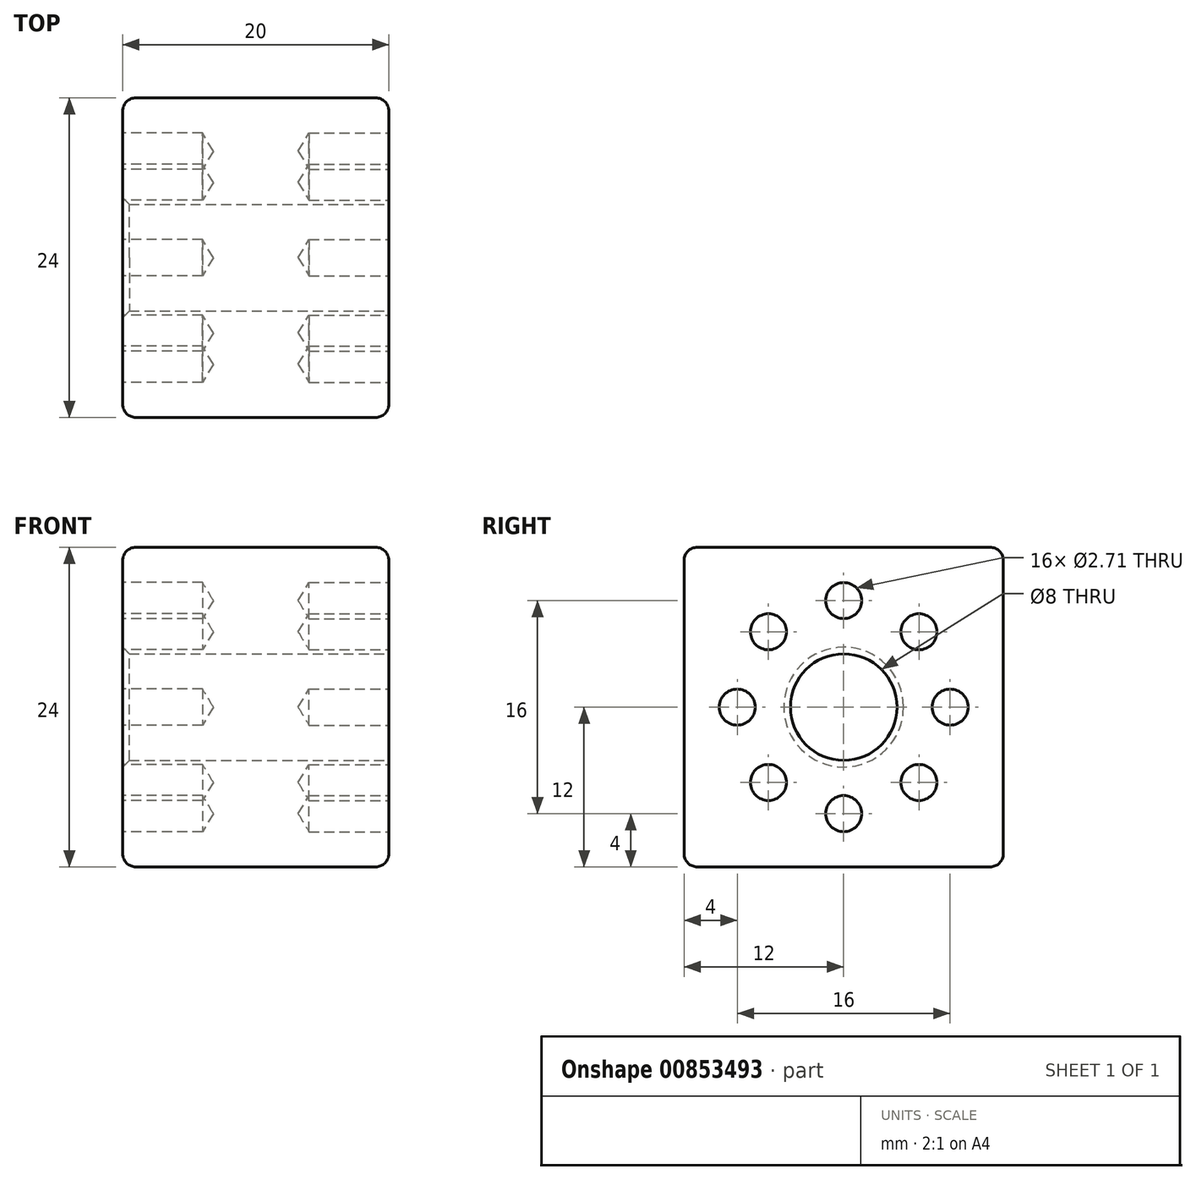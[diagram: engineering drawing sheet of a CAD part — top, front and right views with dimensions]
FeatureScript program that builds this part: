
annotation { "Feature Type Name" : "Feature", "Feature Type Description" : "" }
export const myFeature = defineFeature(function(context is Context, id is Id, definition is map)
    precondition{}
    {
        {
            var Q0;
            Q0=qCreatedBy(makeId("Top.planeOp"),FACE);
            var sketch = newSketch(context, id + "F0", { "sketchPlane" : qUnion([Q0])});
            skLineSegment(sketch, "E0.bottom", {"start": v(10, -12) * mm, "end": v(-10, -12) * mm});
            skLineSegment(sketch, "E0.top", {"start": v(10, 12) * mm, "end": v(-10, 12) * mm});
            skLineSegment(sketch, "E0.left", {"start": v(10, -12) * mm, "end": v(10, 12) * mm});
            skLineSegment(sketch, "E0.right", {"start": v(-10, -12) * mm, "end": v(-10, 12) * mm});
            skPoint(sketch, "E0.middle", {"position": v(0, 0) * mm});
            skSolve(sketch);
        }
        {
            var Q0;
            Q0 = qSketchRegion(id + "F0", true);
            extrude(context, id + "F1", {"entities" : qUnion([Q0]), "depth" : 24 * mm, "offsetDistance" : 25.4 * mm});
        }
        {
            var Q0;
            Q0=makeQuery(id+"F1.opExtrude","SWEPT_FACE",FACE,{"disambiguationData":[OSD([sQuery(id+"F0.wireOp",EDGE,"E0.left")])]});
            var sketch = newSketch(context, id + "F2", { "sketchPlane" : qUnion([Q0])});
            skCircle(sketch, "E1", {"center": v(0, 12) * mm, "radius": 4 * mm});
            skSolve(sketch);
        }
        {
            var Q0;
            Q0 = qSketchRegion(id + "F2", true);
            extrude(context, id + "F3", {"entities" : qUnion([Q0]), "operationType" : NewBodyOperationType.REMOVE, "endBound" : BoundingType.THROUGH_ALL, "oppositeDirection" : true, "depth" : 20 * mm, "offsetDistance" : 25.4 * mm});
        }
        {
            var Q0;
            Q0=makeQuery(id+"F1.opExtrude","SWEPT_FACE",FACE,{"disambiguationData":[OSD([sQuery(id+"F0.wireOp",EDGE,"E0.left")])]});
            var sketch = newSketch(context, id + "F4", { "sketchPlane" : qUnion([Q0])});
            skCircle(sketch, "E2.cCircle", {"center": v(0, 12) * mm, "radius": 8 * mm, "construction": true});
            skLineSegment(sketch, "E2.0", {"start": v(0, 4) * mm, "end": v(-5.66, 6.34) * mm, "construction": true});
            skLineSegment(sketch, "E2.1", {"start": v(-5.66, 6.34) * mm, "end": v(-8, 12) * mm, "construction": true});
            skLineSegment(sketch, "E2.2", {"start": v(-8, 12) * mm, "end": v(-5.66, 17.66) * mm, "construction": true});
            skLineSegment(sketch, "E2.3", {"start": v(-5.66, 17.66) * mm, "end": v(0, 20) * mm, "construction": true});
            skLineSegment(sketch, "E2.4", {"start": v(0, 20) * mm, "end": v(5.66, 17.66) * mm, "construction": true});
            skLineSegment(sketch, "E2.5", {"start": v(5.66, 17.66) * mm, "end": v(8, 12) * mm, "construction": true});
            skLineSegment(sketch, "E2.6", {"start": v(8, 12) * mm, "end": v(5.66, 6.34) * mm, "construction": true});
            skLineSegment(sketch, "E2.7", {"start": v(5.66, 6.34) * mm, "end": v(0, 4) * mm, "construction": true});
            skPoint(sketch, "E3", {"position": v(0, 20) * mm});
            skPoint(sketch, "E4", {"position": v(5.66, 17.66) * mm});
            skPoint(sketch, "E5", {"position": v(8, 12) * mm});
            skPoint(sketch, "E6", {"position": v(5.66, 6.34) * mm});
            skPoint(sketch, "E7", {"position": v(0, 4) * mm});
            skPoint(sketch, "E8", {"position": v(-5.66, 6.34) * mm});
            skPoint(sketch, "E9", {"position": v(-8, 12) * mm});
            skPoint(sketch, "E10", {"position": v(-5.66, 17.66) * mm});
            skSolve(sketch);
        }
        {
            var Q0;
            Q0=sQuery(id+"F4.wireOp",VERTEX,"E3");
            var Q1;
            Q1=sQuery(id+"F4.wireOp",VERTEX,"E4");
            var Q2;
            Q2=sQuery(id+"F4.wireOp",VERTEX,"E5");
            var Q3;
            Q3=sQuery(id+"F4.wireOp",VERTEX,"E6");
            var Q4;
            Q4=sQuery(id+"F4.wireOp",VERTEX,"E7");
            var Q5;
            Q5=sQuery(id+"F4.wireOp",VERTEX,"E8");
            var Q6;
            Q6=sQuery(id+"F4.wireOp",VERTEX,"E9");
            var Q7;
            Q7=sQuery(id+"F4.wireOp",VERTEX,"E10");
            var Q8;
            Q8=makeQuery(id+"F1.opExtrude","SWEPT_BODY",BODY,{"disambiguationData":[OSD([sQuery(id+"F0.wireOp",EDGE,"E0.bottom"),sQuery(id+"F0.wireOp",EDGE,"E0.top"),sQuery(id+"F0.wireOp",EDGE,"E0.left"),sQuery(id+"F0.wireOp",EDGE,"E0.right")])]});
            hole(context, id + "F5", {"style" : HoleStyle.SIMPLE, "endStyle" : HoleEndStyle.BLIND, "standardTappedOrClearance" : lookupTablePath({ "standard" : "ANSI", "engagement" : "75%", "pitch" : "32 tpi", "size" : "#6", "type" : "Tapped" }), "standardBlindInLast" : lookupTablePath({ "standard" : "ANSI", "engagement" : "75%", "pitch" : "32 tpi", "size" : "#6", "type" : "Tapped" }), "holeDiameter" : 2.7 * mm, "majorDiameter" : 3.5 * mm, "showTappedDepth" : true, "holeDepth" : 6 * mm, "isTappedThrough" : true, "tappedDepth" : 3.62 * mm, "tapClearance" : 3, "locations" : qUnion([Q0, Q1, Q2, Q3, Q4, Q5, Q6, Q7]), "scope" : qUnion([Q8])});
        }
        {
            var Q0;
            Q0=makeQuery(id+"F1.opExtrude","SWEPT_FACE",FACE,{"disambiguationData":[OSD([sQuery(id+"F0.wireOp",EDGE,"E0.right")])]});
            var sketch = newSketch(context, id + "F6", { "sketchPlane" : qUnion([Q0])});
            skCircle(sketch, "E11.cCircle", {"center": v(0, 12) * mm, "radius": 8 * mm, "construction": true});
            skLineSegment(sketch, "E11.0", {"start": v(0, 4) * mm, "end": v(-5.66, 6.34) * mm, "construction": true});
            skLineSegment(sketch, "E11.1", {"start": v(-5.66, 6.34) * mm, "end": v(-8, 12) * mm, "construction": true});
            skLineSegment(sketch, "E11.2", {"start": v(-8, 12) * mm, "end": v(-5.66, 17.66) * mm, "construction": true});
            skLineSegment(sketch, "E11.3", {"start": v(-5.66, 17.66) * mm, "end": v(0, 20) * mm, "construction": true});
            skLineSegment(sketch, "E11.4", {"start": v(0, 20) * mm, "end": v(5.66, 17.66) * mm, "construction": true});
            skLineSegment(sketch, "E11.5", {"start": v(5.66, 17.66) * mm, "end": v(8, 12) * mm, "construction": true});
            skLineSegment(sketch, "E11.6", {"start": v(8, 12) * mm, "end": v(5.66, 6.34) * mm, "construction": true});
            skLineSegment(sketch, "E11.7", {"start": v(5.66, 6.34) * mm, "end": v(0, 4) * mm, "construction": true});
            skPoint(sketch, "E12", {"position": v(0, 20) * mm});
            skPoint(sketch, "E13", {"position": v(5.66, 17.66) * mm});
            skPoint(sketch, "E14", {"position": v(8, 12) * mm});
            skPoint(sketch, "E15", {"position": v(5.66, 6.34) * mm});
            skPoint(sketch, "E16", {"position": v(0, 4) * mm});
            skPoint(sketch, "E17", {"position": v(-5.66, 6.34) * mm});
            skPoint(sketch, "E18", {"position": v(-8, 12) * mm});
            skPoint(sketch, "E19", {"position": v(-5.66, 17.66) * mm});
            skSolve(sketch);
        }
        {
            var Q0;
            Q0=sQuery(id+"F6.wireOp",VERTEX,"E12");
            var Q1;
            Q1=sQuery(id+"F6.wireOp",VERTEX,"E13");
            var Q2;
            Q2=sQuery(id+"F6.wireOp",VERTEX,"E14");
            var Q3;
            Q3=sQuery(id+"F6.wireOp",VERTEX,"E15");
            var Q4;
            Q4=sQuery(id+"F6.wireOp",VERTEX,"E16");
            var Q5;
            Q5=sQuery(id+"F6.wireOp",VERTEX,"E17");
            var Q6;
            Q6=sQuery(id+"F6.wireOp",VERTEX,"E18");
            var Q7;
            Q7=sQuery(id+"F6.wireOp",VERTEX,"E19");
            var Q8;
            Q8=makeQuery(id+"F1.opExtrude","SWEPT_BODY",BODY,{"disambiguationData":[OSD([sQuery(id+"F0.wireOp",EDGE,"E0.bottom"),sQuery(id+"F0.wireOp",EDGE,"E0.top"),sQuery(id+"F0.wireOp",EDGE,"E0.left"),sQuery(id+"F0.wireOp",EDGE,"E0.right")])]});
            hole(context, id + "F7", {"style" : HoleStyle.SIMPLE, "endStyle" : HoleEndStyle.BLIND, "standardTappedOrClearance" : lookupTablePath({ "standard" : "ANSI", "engagement" : "75%", "pitch" : "32 tpi", "size" : "#6", "type" : "Tapped" }), "standardBlindInLast" : lookupTablePath({ "standard" : "ANSI", "engagement" : "75%", "pitch" : "32 tpi", "size" : "#6", "type" : "Tapped" }), "holeDiameter" : 2.7 * mm, "majorDiameter" : 3.5 * mm, "showTappedDepth" : true, "holeDepth" : 6 * mm, "isTappedThrough" : true, "tappedDepth" : 3.62 * mm, "tapClearance" : 3, "locations" : qUnion([Q0, Q1, Q2, Q3, Q4, Q5, Q6, Q7]), "scope" : qUnion([Q8])});
        }
        {
            var Q0;
            Q0=makeQuery(id+"F1.opExtrude","CAP_FACE",FACE,{"disambiguationData":[OSD([sQuery(id+"F0.wireOp",EDGE,"E0.bottom"),sQuery(id+"F0.wireOp",EDGE,"E0.top"),sQuery(id+"F0.wireOp",EDGE,"E0.left"),sQuery(id+"F0.wireOp",EDGE,"E0.right")])],"isStart":false});
            var Q1;
            Q1=makeQuery(id+"F1.opExtrude","SWEPT_FACE",FACE,{"disambiguationData":[OSD([sQuery(id+"F0.wireOp",EDGE,"E0.bottom")])]});
            var Q2;
            Q2=makeQuery(id+"F1.opExtrude","SWEPT_FACE",FACE,{"disambiguationData":[OSD([sQuery(id+"F0.wireOp",EDGE,"E0.top")])]});
            var Q3;
            Q3=makeQuery(id+"F1.opExtrude","CAP_FACE",FACE,{"disambiguationData":[OSD([sQuery(id+"F0.wireOp",EDGE,"E0.bottom"),sQuery(id+"F0.wireOp",EDGE,"E0.top"),sQuery(id+"F0.wireOp",EDGE,"E0.left"),sQuery(id+"F0.wireOp",EDGE,"E0.right")])],"isStart":true});
            fillet(context, id + "F8", {"entities" : qUnion([Q0, Q1, Q2, Q3]), "radius" : 1 * mm, "tangentPropagation" : true, "allowEdgeOverflow" : false});
        }
        {
            var Q0;
            Q0=makeQuery(id+"F3.boolean.opBoolean","COPY",EDGE,{"derivedFrom":makeQuery(id+"F3.opExtrude","CAP_EDGE",EDGE,{"disambiguationData":[OSD([sQuery(id+"F2.wireOp",EDGE,"E1")])],"isStart":true})});
            var Q1;
            Q1=makeQuery(id+"F5.hole-0.boolean.opBoolean","COPY",EDGE,{"derivedFrom":makeQuery(id+"F5.hole-0.opRevolve","SWEPT_EDGE",EDGE,{"disambiguationData":[OSD([sQuery(id+"F5.hole-0.sketch.wireOp",EDGE,"core_line_2"),sQuery(id+"F5.hole-0.sketch.wireOp",EDGE,"core_line_3")])]})});
            var Q2;
            Q2=makeQuery(id+"F5.hole-1.boolean.opBoolean","COPY",EDGE,{"derivedFrom":makeQuery(id+"F5.hole-1.opRevolve","SWEPT_EDGE",EDGE,{"disambiguationData":[OSD([sQuery(id+"F5.hole-1.sketch.wireOp",EDGE,"core_line_2"),sQuery(id+"F5.hole-1.sketch.wireOp",EDGE,"core_line_3")])]})});
            var Q3;
            Q3=makeQuery(id+"F5.hole-2.boolean.opBoolean","COPY",EDGE,{"derivedFrom":makeQuery(id+"F5.hole-2.opRevolve","SWEPT_EDGE",EDGE,{"disambiguationData":[OSD([sQuery(id+"F5.hole-2.sketch.wireOp",EDGE,"core_line_2"),sQuery(id+"F5.hole-2.sketch.wireOp",EDGE,"core_line_3")])]})});
            var Q4;
            Q4=makeQuery(id+"F5.hole-3.boolean.opBoolean","COPY",EDGE,{"derivedFrom":makeQuery(id+"F5.hole-3.opRevolve","SWEPT_EDGE",EDGE,{"disambiguationData":[OSD([sQuery(id+"F5.hole-3.sketch.wireOp",EDGE,"core_line_2"),sQuery(id+"F5.hole-3.sketch.wireOp",EDGE,"core_line_3")])]})});
            var Q5;
            Q5=makeQuery(id+"F5.hole-4.boolean.opBoolean","COPY",EDGE,{"derivedFrom":makeQuery(id+"F5.hole-4.opRevolve","SWEPT_EDGE",EDGE,{"disambiguationData":[OSD([sQuery(id+"F5.hole-4.sketch.wireOp",EDGE,"core_line_2"),sQuery(id+"F5.hole-4.sketch.wireOp",EDGE,"core_line_3")])]})});
            var Q6;
            Q6=makeQuery(id+"F5.hole-5.boolean.opBoolean","COPY",EDGE,{"derivedFrom":makeQuery(id+"F5.hole-5.opRevolve","SWEPT_EDGE",EDGE,{"disambiguationData":[OSD([sQuery(id+"F5.hole-5.sketch.wireOp",EDGE,"core_line_2"),sQuery(id+"F5.hole-5.sketch.wireOp",EDGE,"core_line_3")])]})});
            var Q7;
            Q7=makeQuery(id+"F5.hole-6.boolean.opBoolean","COPY",EDGE,{"derivedFrom":makeQuery(id+"F5.hole-6.opRevolve","SWEPT_EDGE",EDGE,{"disambiguationData":[OSD([sQuery(id+"F5.hole-6.sketch.wireOp",EDGE,"core_line_2"),sQuery(id+"F5.hole-6.sketch.wireOp",EDGE,"core_line_3")])]})});
            var Q8;
            Q8=makeQuery(id+"F5.hole-7.boolean.opBoolean","COPY",EDGE,{"derivedFrom":makeQuery(id+"F5.hole-7.opRevolve","SWEPT_EDGE",EDGE,{"disambiguationData":[OSD([sQuery(id+"F5.hole-7.sketch.wireOp",EDGE,"core_line_2"),sQuery(id+"F5.hole-7.sketch.wireOp",EDGE,"core_line_3")])]})});
            var Q9;
            Q9=makeQuery(id+"F7.hole-6.boolean.opBoolean","COPY",EDGE,{"derivedFrom":makeQuery(id+"F7.hole-6.opRevolve","SWEPT_EDGE",EDGE,{"disambiguationData":[OSD([sQuery(id+"F7.hole-6.sketch.wireOp",EDGE,"core_line_2"),sQuery(id+"F7.hole-6.sketch.wireOp",EDGE,"core_line_3")])]})});
            var Q10;
            Q10=makeQuery(id+"F7.hole-7.boolean.opBoolean","COPY",EDGE,{"derivedFrom":makeQuery(id+"F7.hole-7.opRevolve","SWEPT_EDGE",EDGE,{"disambiguationData":[OSD([sQuery(id+"F7.hole-7.sketch.wireOp",EDGE,"core_line_2"),sQuery(id+"F7.hole-7.sketch.wireOp",EDGE,"core_line_3")])]})});
            var Q11;
            Q11=makeQuery(id+"F7.hole-0.boolean.opBoolean","COPY",EDGE,{"derivedFrom":makeQuery(id+"F7.hole-0.opRevolve","SWEPT_EDGE",EDGE,{"disambiguationData":[OSD([sQuery(id+"F7.hole-0.sketch.wireOp",EDGE,"core_line_2"),sQuery(id+"F7.hole-0.sketch.wireOp",EDGE,"core_line_3")])]})});
            var Q12;
            Q12=makeQuery(id+"F7.hole-1.boolean.opBoolean","COPY",EDGE,{"derivedFrom":makeQuery(id+"F7.hole-1.opRevolve","SWEPT_EDGE",EDGE,{"disambiguationData":[OSD([sQuery(id+"F7.hole-1.sketch.wireOp",EDGE,"core_line_2"),sQuery(id+"F7.hole-1.sketch.wireOp",EDGE,"core_line_3")])]})});
            var Q13;
            Q13=makeQuery(id+"F7.hole-2.boolean.opBoolean","COPY",EDGE,{"derivedFrom":makeQuery(id+"F7.hole-2.opRevolve","SWEPT_EDGE",EDGE,{"disambiguationData":[OSD([sQuery(id+"F7.hole-2.sketch.wireOp",EDGE,"core_line_2"),sQuery(id+"F7.hole-2.sketch.wireOp",EDGE,"core_line_3")])]})});
            var Q14;
            Q14=makeQuery(id+"F7.hole-3.boolean.opBoolean","COPY",EDGE,{"derivedFrom":makeQuery(id+"F7.hole-3.opRevolve","SWEPT_EDGE",EDGE,{"disambiguationData":[OSD([sQuery(id+"F7.hole-3.sketch.wireOp",EDGE,"core_line_2"),sQuery(id+"F7.hole-3.sketch.wireOp",EDGE,"core_line_3")])]})});
            var Q15;
            Q15=makeQuery(id+"F7.hole-4.boolean.opBoolean","COPY",EDGE,{"derivedFrom":makeQuery(id+"F7.hole-4.opRevolve","SWEPT_EDGE",EDGE,{"disambiguationData":[OSD([sQuery(id+"F7.hole-4.sketch.wireOp",EDGE,"core_line_2"),sQuery(id+"F7.hole-4.sketch.wireOp",EDGE,"core_line_3")])]})});
            var Q16;
            Q16=makeQuery(id+"F7.hole-5.boolean.opBoolean","COPY",EDGE,{"derivedFrom":makeQuery(id+"F7.hole-5.opRevolve","SWEPT_EDGE",EDGE,{"disambiguationData":[OSD([sQuery(id+"F7.hole-5.sketch.wireOp",EDGE,"core_line_2"),sQuery(id+"F7.hole-5.sketch.wireOp",EDGE,"core_line_3")])]})});
            var Q17;
            Q17=makeQuery(id+"F3.boolean.opBoolean","INTERSECT",EDGE,{"derivedFrom":[makeQuery(id+"F1.opExtrude","SWEPT_FACE",FACE,{"disambiguationData":[OSD([sQuery(id+"F0.wireOp",EDGE,"E0.right")])]}),makeQuery(id+"F3.opExtrude","SWEPT_FACE",FACE,{"disambiguationData":[OSD([sQuery(id+"F2.wireOp",EDGE,"E1")])]})]});
            chamfer(context, id + "F9", {"entities" : qUnion([Q0, Q1, Q2, Q3, Q4, Q5, Q6, Q7, Q8, Q9, Q10, Q11, Q12, Q13, Q14, Q15, Q16, Q17]), "width" : .5 * mm, "tangentPropagation" : true});
        }
    });
